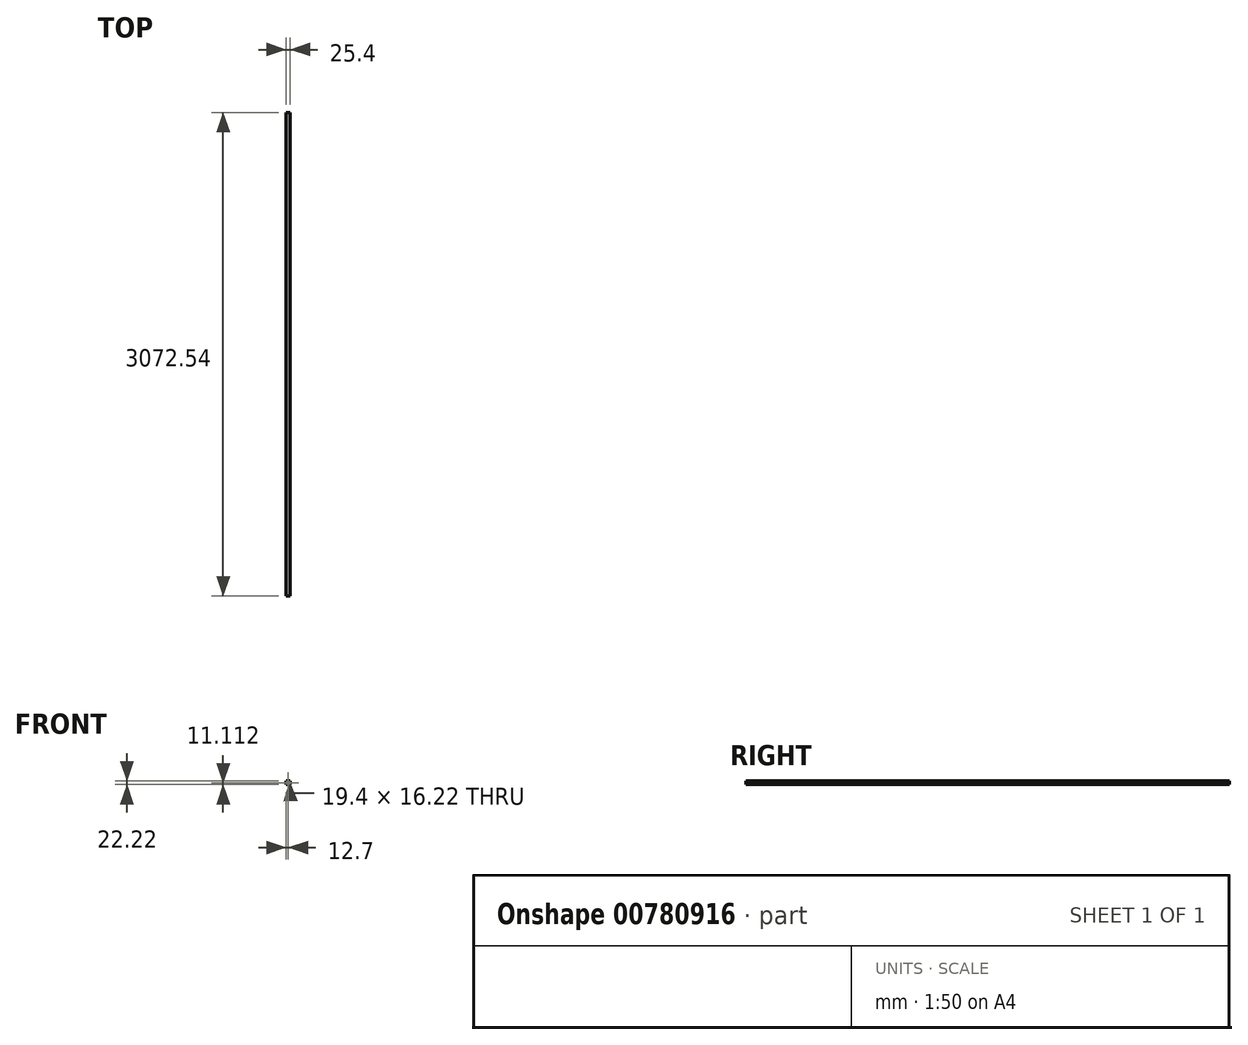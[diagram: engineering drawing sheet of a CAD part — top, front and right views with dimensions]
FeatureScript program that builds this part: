
annotation { "Feature Type Name" : "Feature", "Feature Type Description" : "" }
export const myFeature = defineFeature(function(context is Context, id is Id, definition is map)
    precondition{}
    {
        {
            var Q0;
            Q0=qCreatedBy(makeId("Right.planeOp"),FACE);
            var sketch = newSketch(context, id + "F0", { "sketchPlane" : qUnion([Q0])});
            skLineSegment(sketch, "E0", {"start": v(-75.34, 0) * mm, "end": v(-75.34, -22.22) * mm});
            skLineSegment(sketch, "E1", {"start": v(-75.34, -22.22) * mm, "end": v(0, -22.22) * mm});
            skLineSegment(sketch, "E2", {"start": v(0, -22.22) * mm, "end": v(0, 0) * mm});
            skLineSegment(sketch, "E3", {"start": v(0, 0) * mm, "end": v(-75.34, 0) * mm});
            skSolve(sketch);
        }
        {
            var Q0;
            Q0=makeQuery(id+"F0.imprint","IMPRINT",FACE,{"disambiguationData":[TD([[makeQuery(id+"F0.imprint","IMPRINT",EDGE,{"derivedFrom":sQuery(id+"F0.wireOp",EDGE,"E0")}),1.0]])]});
            extrude(context, id + "F1", {"entities" : qUnion([Q0]), "depth" : 25.4 * mm, "offsetDistance" : 25.4 * mm});
        }
        {
            var Q0;
            Q0=makeQuery(id+"F1.opExtrude","SWEPT_FACE",FACE,{"disambiguationData":[OSD([sQuery(id+"F0.wireOp",EDGE,"E0")])]});
            var Q1;
            Q1=makeQuery(id+"F1.opExtrude","SWEPT_FACE",FACE,{"disambiguationData":[OSD([sQuery(id+"F0.wireOp",EDGE,"E2")])]});
            shell(context, id + "F2", {"entities" : qUnion([Q0, Q1]), "thickness" : 3 * mm});
        }
        {
            var Q0;
            Q0=makeQuery(id+"F1.opExtrude","SWEPT_FACE",FACE,{"disambiguationData":[OSD([sQuery(id+"F0.wireOp",EDGE,"E2")])]});
            extrude(context, id + "F3", {"entities" : qUnion([Q0]), "operationType" : NewBodyOperationType.ADD, "depth" : 2997.2 * mm, "offsetDistance" : 25.4 * mm});
        }
    });
